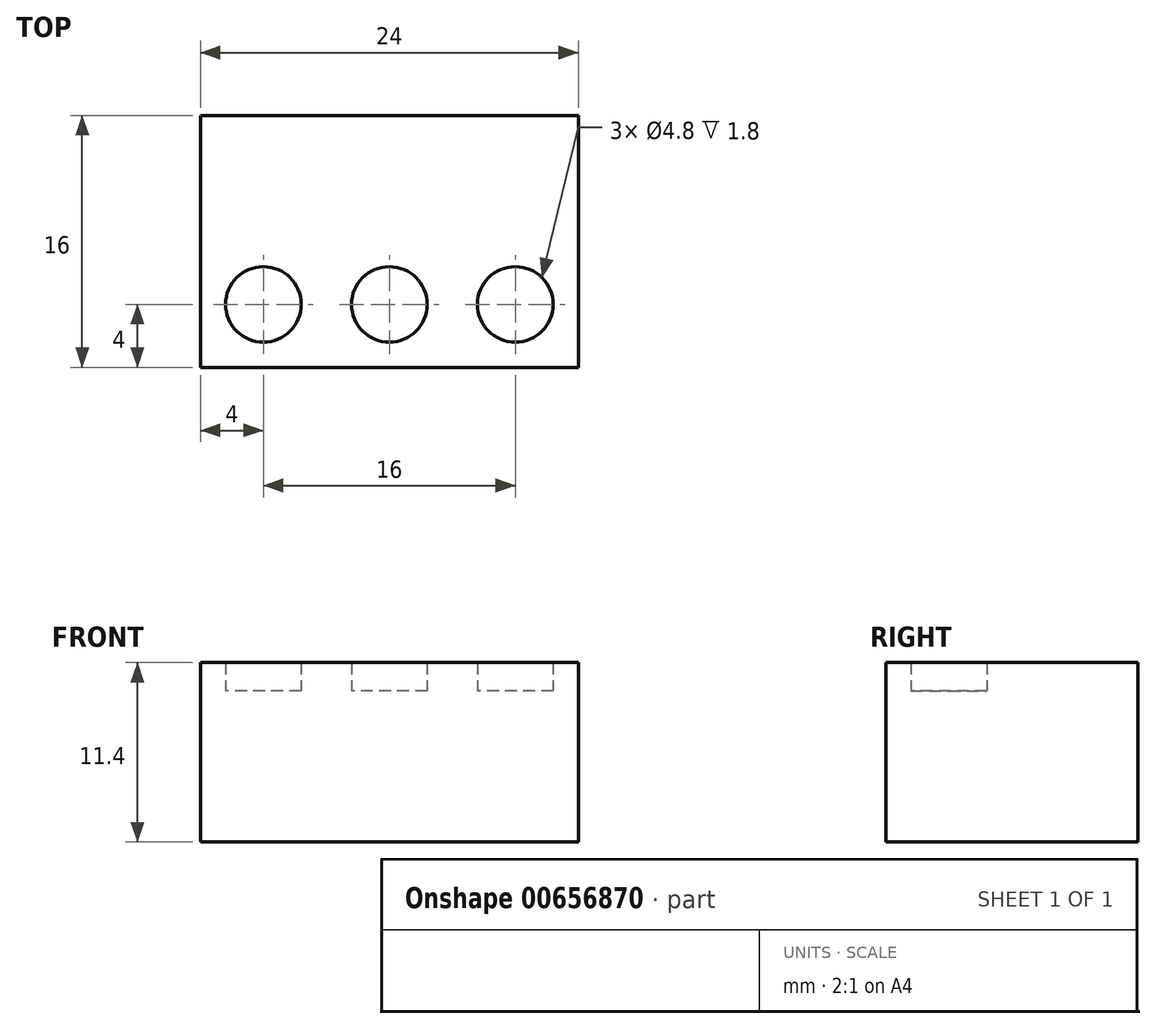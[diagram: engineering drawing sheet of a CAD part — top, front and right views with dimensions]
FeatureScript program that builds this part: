
annotation { "Feature Type Name" : "Feature", "Feature Type Description" : "" }
export const myFeature = defineFeature(function(context is Context, id is Id, definition is map)
    precondition{}
    {
        {
            var Q0;
            Q0=qCreatedBy(makeId("Top.planeOp"),FACE);
            var sketch = newSketch(context, id + "F0", { "sketchPlane" : qUnion([Q0])});
            skLineSegment(sketch, "E0.bottom", {"start": v(0, 0) * mm, "end": v(-24, 0) * mm});
            skLineSegment(sketch, "E0.top", {"start": v(0, 16) * mm, "end": v(-24, 16) * mm});
            skLineSegment(sketch, "E0.left", {"start": v(0, 0) * mm, "end": v(0, 16) * mm});
            skLineSegment(sketch, "E0.right", {"start": v(-24, 0) * mm, "end": v(-24, 16) * mm});
            skSolve(sketch);
        }
        {
            var Q0;
            Q0=makeQuery(id+"F0.imprint","IMPRINT",FACE,{"disambiguationData":[TD([[makeQuery(id+"F0.imprint","IMPRINT",EDGE,{"derivedFrom":sQuery(id+"F0.wireOp",EDGE,"E0.bottom")}),-1.0]])]});
            extrude(context, id + "F1", {"entities" : qUnion([Q0]), "depth" : 9.6 * mm, "offsetDistance" : 25.4 * mm});
        }
        {
            var Q0;
            Q0=makeQuery(id+"F1.opExtrude","CAP_FACE",FACE,{"disambiguationData":[OSD([sQuery(id+"F0.wireOp",EDGE,"E0.bottom"),sQuery(id+"F0.wireOp",EDGE,"E0.top"),sQuery(id+"F0.wireOp",EDGE,"E0.left"),sQuery(id+"F0.wireOp",EDGE,"E0.right")])],"isStart":false});
            var sketch = newSketch(context, id + "F2", { "sketchPlane" : qUnion([Q0])});
            skCircle(sketch, "E1", {"center": v(-20, 12) * mm, "radius": 2.4 * mm});
            skCircle(sketch, "E2", {"center": v(-4, 12) * mm, "radius": 2.4 * mm});
            skCircle(sketch, "E3", {"center": v(-12, 12) * mm, "radius": 2.4 * mm});
            skCircle(sketch, "E4.MirrorC", {"center": v(-20, 4) * mm, "radius": 2.4 * mm});
            skCircle(sketch, "E5.MirrorC", {"center": v(-12, 4) * mm, "radius": 2.4 * mm});
            skCircle(sketch, "E6.MirrorC", {"center": v(-4, 4) * mm, "radius": 2.4 * mm});
            skSolve(sketch);
        }
        {
            var Q0;
            Q0=makeQuery(id+"F2.imprint","IMPRINT",FACE,{"disambiguationData":[TD([[makeQuery(id+"F2.imprint","IMPRINT",EDGE,{"derivedFrom":sQuery(id+"F2.wireOp",EDGE,"E1")}),1.0]])]});
            var Q1;
            Q1=makeQuery(id+"F2.imprint","IMPRINT",FACE,{"disambiguationData":[TD([[makeQuery(id+"F2.imprint","IMPRINT",EDGE,{"derivedFrom":sQuery(id+"F2.wireOp",EDGE,"E3")}),1.0]])]});
            var Q2;
            Q2=makeQuery(id+"F2.imprint","IMPRINT",FACE,{"disambiguationData":[TD([[makeQuery(id+"F2.imprint","IMPRINT",EDGE,{"derivedFrom":sQuery(id+"F2.wireOp",EDGE,"E2")}),1.0]])]});
            var Q3;
            Q3=makeQuery(id+"F2.imprint","IMPRINT",FACE,{"disambiguationData":[TD([[makeQuery(id+"F2.imprint","IMPRINT",EDGE,{"derivedFrom":sQuery(id+"F2.wireOp",EDGE,"E6.MirrorC")}),-1.0]])]});
            var Q4;
            Q4=makeQuery(id+"F2.imprint","IMPRINT",FACE,{"disambiguationData":[TD([[makeQuery(id+"F2.imprint","IMPRINT",EDGE,{"derivedFrom":sQuery(id+"F2.wireOp",EDGE,"E5.MirrorC")}),-1.0]])]});
            var Q5;
            Q5=makeQuery(id+"F2.imprint","IMPRINT",FACE,{"disambiguationData":[TD([[makeQuery(id+"F2.imprint","IMPRINT",EDGE,{"derivedFrom":sQuery(id+"F2.wireOp",EDGE,"E4.MirrorC")}),-1.0]])]});
            extrude(context, id + "F3", {"entities" : qUnion([Q0, Q1, Q2, Q3, Q4, Q5]), "operationType" : NewBodyOperationType.ADD, "depth" : 1.8 * mm, "offsetDistance" : 25.4 * mm});
        }
    });
